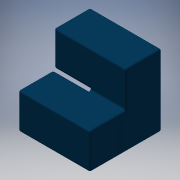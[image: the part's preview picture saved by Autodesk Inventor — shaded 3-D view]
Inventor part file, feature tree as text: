
AUTODESK INVENTOR PART (.ipt)
format: ipt  version: 2016 (Build 200138000, 138)  size: 237,056 bytes
history: native  units: in
note: dims shown in document units (in); Inventor stores cm internally (conversion verified against a paired STEP export)
features: plane x8, fillet x6, extrude x3, other x1, sketch x1
ambient origin geometry x8: Origin, YZ Plane, XZ Plane, XY Plane, X Axis, Y Axis, Z Axis, Center Point
bodies: Body1 (feature_tree)
feature tree (19):
  other  "Cube Master.ipt"
  extrude  "Extrusion4"  Depth=0.3937in
  extrude  "Extrusion5"  Depth=0.374in
  fillet  "Fillet1"  [1 undecoded]
  extrude  "Extrusion6"  Depth=0.374in
  fillet  "Fillet2"  [1 undecoded]
  fillet  "Fillet3"  Radius=0.374in
  fillet  "Fillet4"  [1 undecoded]
  fillet  "Fillet7"  Radius=0.0386in
  fillet  "Fillet8"  Radius=0.0386in
  sketch  "Sketch1"  dims[d0=0.3937in d1=0.3937in d9=0.374in d10=0.0in d11=0.374in d12=0.0in d13=0.374in d14=0.0in d15=0.0386in d16=0.0386in d18=0.0193in d19=0.0193in d22=0.0193in d23=0.0096in]
  plane  "Work Plane1"
  plane  "Work Plane2"
  plane  "Work Plane3"
  plane  "Work Plane4"
  plane  "Work Plane5"
  plane  "Work Plane6"
  plane  "Work Plane7"
  plane  "Work Plane8"
note: 3 required parameter values undecoded (feature->parameter linkage not recoverable at this tier; creation-order binding heuristic only, values carry confidence <= 0.55)
